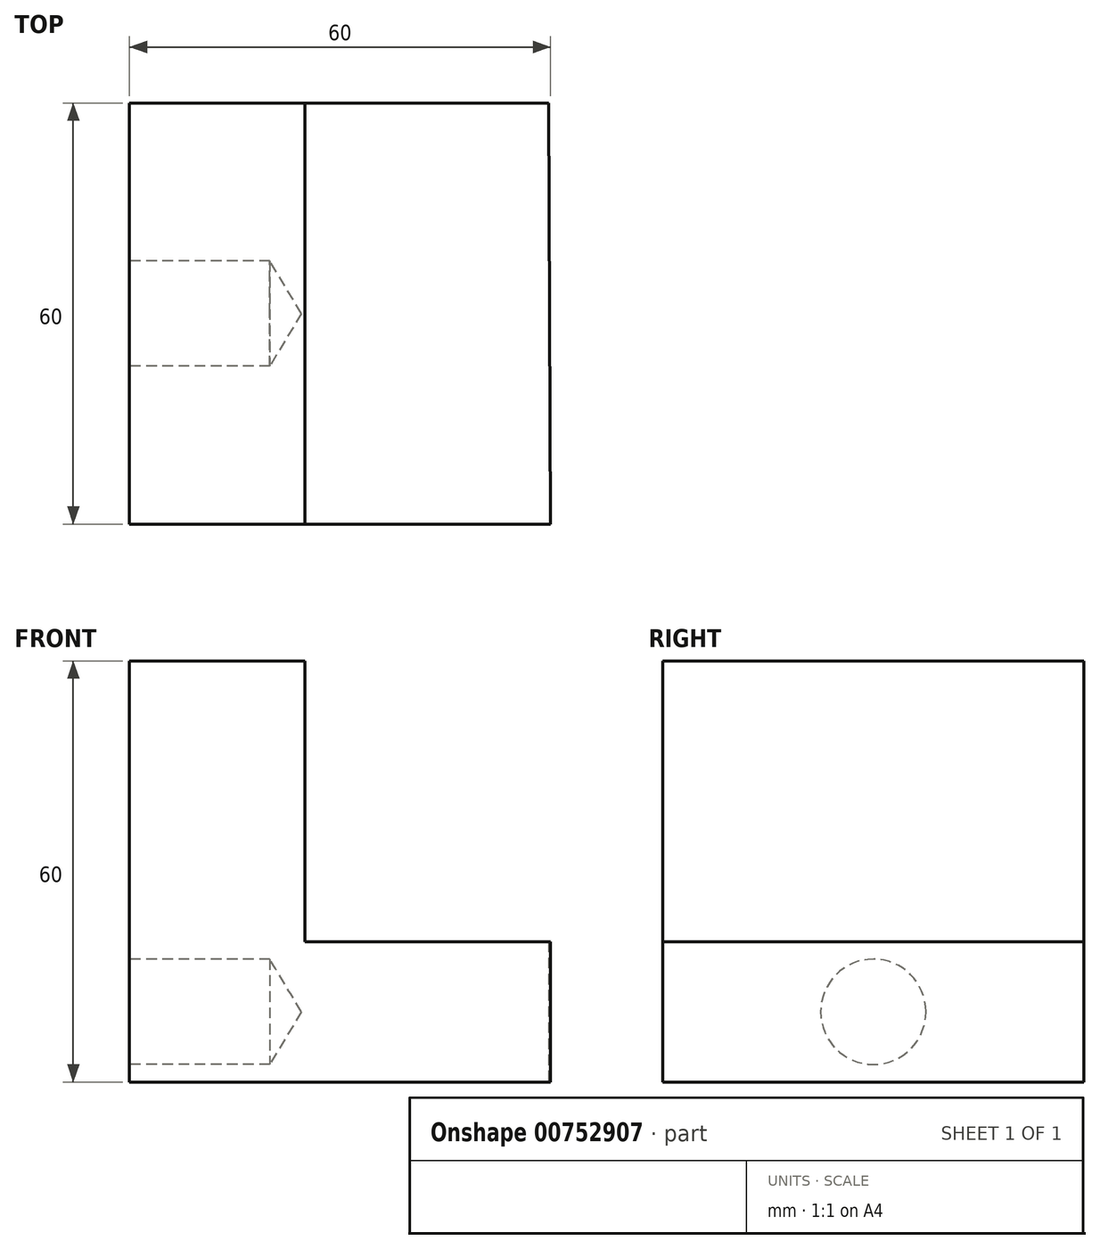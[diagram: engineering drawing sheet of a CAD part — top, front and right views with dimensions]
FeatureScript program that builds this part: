
annotation { "Feature Type Name" : "Feature", "Feature Type Description" : "" }
export const myFeature = defineFeature(function(context is Context, id is Id, definition is map)
    precondition{}
    {
        {
            var Q0;
            Q0=qCreatedBy(makeId("Top.planeOp"),FACE);
            var sketch = newSketch(context, id + "F0", { "sketchPlane" : qUnion([Q0])});
            skLineSegment(sketch, "E0.bottom", {"start": v(-30, -30) * mm, "end": v(-5, -30) * mm});
            skLineSegment(sketch, "E0.top", {"start": v(-30, 30) * mm, "end": v(-5, 30) * mm});
            skLineSegment(sketch, "E0.left", {"start": v(-30, -30) * mm, "end": v(-30, 30) * mm});
            skPoint(sketch, "E0.middle", {"position": v(0, 0) * mm});
            skLineSegment(sketch, "E1", {"start": v(-5, 30) * mm, "end": v(-5, -30) * mm});
            skPoint(sketch, "E0.right.end.orphan", {"position": v(30, 30) * mm});
            skPoint(sketch, "E2.orphan", {"position": v(30, -30) * mm});
            skSolve(sketch);
        }
        {
            var Q0;
            Q0 = qSketchRegion(id + "F0", true);
            extrude(context, id + "F1", {"entities" : qUnion([Q0]), "depth" : 60 * mm, "offsetDistance" : 25 * mm});
        }
        {
            var Q0;
            Q0=qCreatedBy(makeId("Top.planeOp"),FACE);
            var sketch = newSketch(context, id + "F2", { "sketchPlane" : qUnion([Q0])});
            skLineSegment(sketch, "E3", {"start": v(-5.26, 30) * mm, "end": v(29.74, 30) * mm});
            skLineSegment(sketch, "E4", {"start": v(-5, -30) * mm, "end": v(30, -30) * mm});
            skLineSegment(sketch, "E5", {"start": v(30, -30) * mm, "end": v(29.74, 30) * mm});
            skLineSegment(sketch, "E6", {"start": v(-5.26, 30) * mm, "end": v(-5, -30) * mm});
            skSolve(sketch);
        }
        {
            var Q0;
            Q0 = qSketchRegion(id + "F2", true);
            extrude(context, id + "F3", {"entities" : qUnion([Q0]), "operationType" : NewBodyOperationType.ADD, "depth" : 20 * mm, "offsetDistance" : 25 * mm});
        }
        {
            var Q0;
            Q0=makeQuery(id+"F1.opExtrude","SWEPT_FACE",FACE,{"disambiguationData":[OSD([sQuery(id+"F0.wireOp",EDGE,"E0.left")])]});
            var sketch = newSketch(context, id + "F4", { "sketchPlane" : qUnion([Q0])});
            skCircle(sketch, "E7", {"center": v(0, 10) * mm, "radius": 7.5 * mm});
            skSolve(sketch);
        }
        {
            var Q0;
            Q0=sQuery(id+"F4.wireOp",VERTEX,"E7.center");
            var Q1;
            Q1=makeQuery(id+"F1.opExtrude","SWEPT_BODY",BODY,{"disambiguationData":[OSD([sQuery(id+"F0.wireOp",EDGE,"E0.bottom"),sQuery(id+"F0.wireOp",EDGE,"E0.left"),sQuery(id+"F0.wireOp",EDGE,"E0.top"),sQuery(id+"F0.wireOp",EDGE,"E1")])]});
            hole(context, id + "F5", {"style" : HoleStyle.SIMPLE, "endStyle" : HoleEndStyle.BLIND, "holeDiameter" : 15 * mm, "majorDiameter" : 5 * mm, "holeDepth" : 20 * mm, "isTappedThrough" : true, "tappedDepth" : 12 * mm, "tapClearance" : 3, "locations" : qUnion([Q0]), "scope" : qUnion([Q1])});
        }
    });
